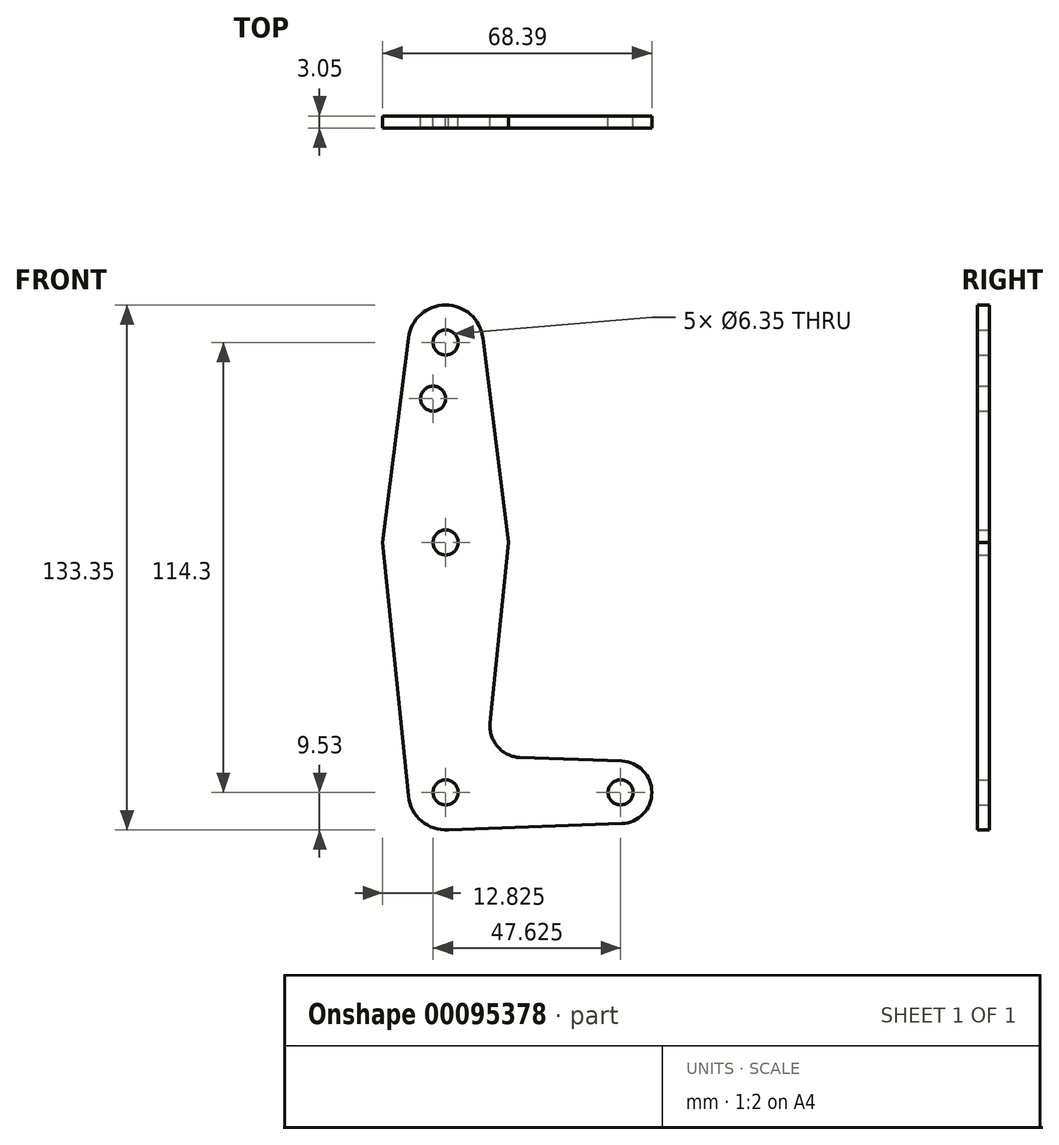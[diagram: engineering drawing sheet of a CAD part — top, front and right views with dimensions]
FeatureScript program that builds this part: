
annotation { "Feature Type Name" : "Feature", "Feature Type Description" : "" }
export const myFeature = defineFeature(function(context is Context, id is Id, definition is map)
    precondition{}
    {
        {
            var Q0;
            Q0=qCreatedBy(makeId("Front.planeOp"),FACE);
            var sketch = newSketch(context, id + "F0", { "sketchPlane" : qUnion([Q0])});
            skCircle(sketch, "E0", {"center": v(0, 0) * mm, "radius": 15.88 * mm});
            skCircle(sketch, "E1", {"center": v(0, 50.8) * mm, "radius": 9.53 * mm});
            skCircle(sketch, "E2", {"center": v(0, -63.5) * mm, "radius": 9.53 * mm});
            skCircle(sketch, "E3", {"center": v(44.45, -63.5) * mm, "radius": 7.94 * mm});
            skLineSegment(sketch, "E4", {"start": v(0, -63.5) * mm, "end": v(0, 50.8) * mm, "construction": true});
            skLineSegment(sketch, "E5", {"start": v(0, -63.5) * mm, "end": v(44.45, -63.5) * mm, "construction": true});
            skLineSegment(sketch, "E6", {"start": v(-9.45, 52) * mm, "end": v(-16, 0) * mm});
            skLineSegment(sketch, "E7", {"start": v(9.45, 52) * mm, "end": v(16, 0) * mm});
            skLineSegment(sketch, "E8", {"start": v(16, 0) * mm, "end": v(11.32, -45.9) * mm});
            skLineSegment(sketch, "E9", {"start": v(18.95, -54.65) * mm, "end": v(44.73, -55.57) * mm});
            skLineSegment(sketch, "E10", {"start": v(0, -73.03) * mm, "end": v(44.73, -71.43) * mm});
            skLineSegment(sketch, "E11", {"start": v(-16, 0) * mm, "end": v(-9.48, -64.46) * mm});
            skCircle(sketch, "E12", {"center": v(0, 50.8) * mm, "radius": 3.18 * mm});
            skCircle(sketch, "E13", {"center": v(0, 0) * mm, "radius": 3.18 * mm});
            skCircle(sketch, "E14", {"center": v(-3.18, 36.53) * mm, "radius": 3.18 * mm});
            skCircle(sketch, "E15", {"center": v(0, -63.5) * mm, "radius": 3.18 * mm});
            skCircle(sketch, "E16", {"center": v(44.45, -63.5) * mm, "radius": 3.18 * mm});
            skArc(sketch, "E17.filletArc", {"start": v(11.32, -45.9) * mm, "mid": v(13.24, -51.93) * mm, "end": v(18.95, -54.65) * mm});
            skSolve(sketch);
        }
        {
            var Q0;
            Q0 = qSketchRegion(id + "F0", true);
            extrude(context, id + "F1", {"entities" : qUnion([Q0]), "depth" : 3.05 * mm});
        }
    });
